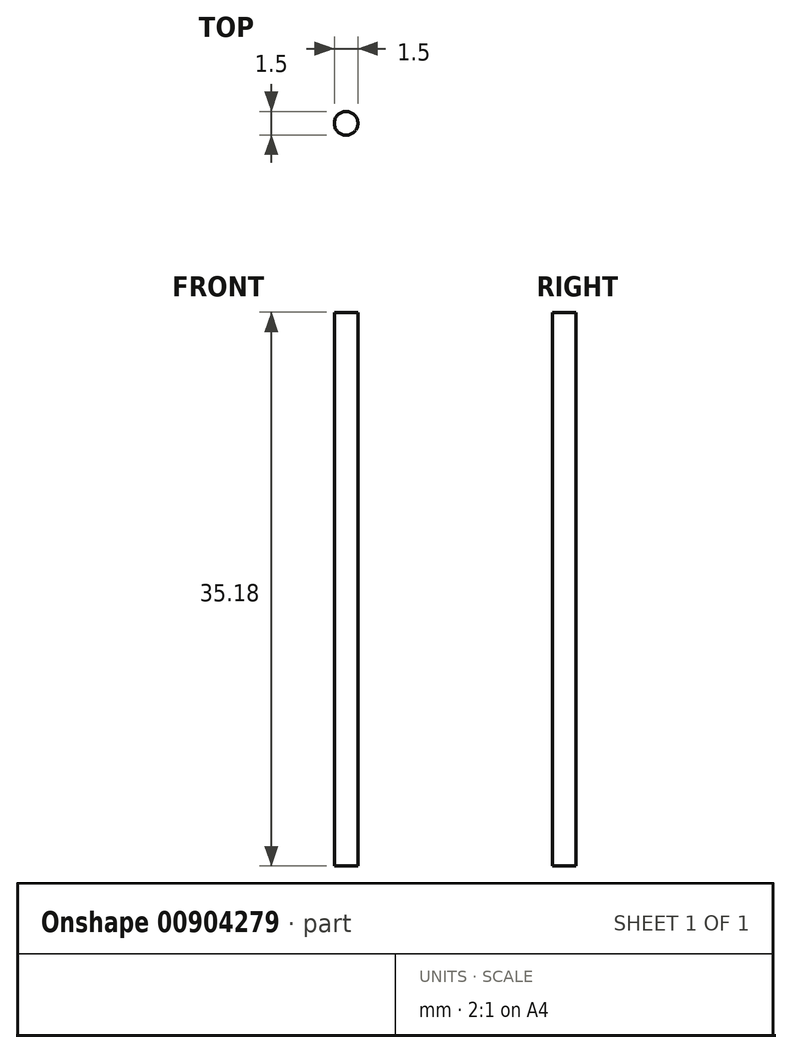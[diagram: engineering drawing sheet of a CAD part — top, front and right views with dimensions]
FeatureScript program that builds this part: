
annotation { "Feature Type Name" : "Feature", "Feature Type Description" : "" }
export const myFeature = defineFeature(function(context is Context, id is Id, definition is map)
    precondition{}
    {
        {
            var Q0;
            Q0=qCreatedBy(makeId("Front.planeOp"),FACE);
            var sketch = newSketch(context, id + "F0", { "sketchPlane" : qUnion([Q0])});
            skLineSegment(sketch, "E0.bottom", {"start": v(0, 0) * mm, "end": v(-0.75, 0) * mm});
            skLineSegment(sketch, "E0.top", {"start": v(0, 34.58) * mm, "end": v(-0.75, 34.58) * mm});
            skLineSegment(sketch, "E0.left", {"start": v(0, 0) * mm, "end": v(0, 34.58) * mm});
            skLineSegment(sketch, "E0.right", {"start": v(-0.75, 0) * mm, "end": v(-0.75, 34.58) * mm});
            skSolve(sketch);
        }
        {
            var Q0;
            Q0=makeQuery(id+"F0.imprint","IMPRINT",FACE,{"disambiguationData":[TD([[makeQuery(id+"F0.imprint","IMPRINT",EDGE,{"derivedFrom":sQuery(id+"F0.wireOp",EDGE,"E0.bottom")}),-1.0]])]});
            var Q1;
            Q1=sQuery(id+"F0.wireOp",EDGE,"E0.left");
            revolve(context, id + "F1", {"surfaceOperationType" : NewSurfaceOperationType.NEW, "entities" : qUnion([Q0]), "axis" : qUnion([Q1]), "revolveType" : RevolveType.FULL});
        }
        {
            var Q0;
            Q0=makeQuery(id+"F1.opRevolve","SWEPT_FACE",FACE,{"disambiguationData":[OSD([sQuery(id+"F0.wireOp",EDGE,"E0.bottom")])]});
            extrude(context, id + "F2", {"entities" : qUnion([Q0]), "operationType" : NewBodyOperationType.ADD, "depth" : 0.6 * mm, "offsetDistance" : 25 * mm});
        }
    });
